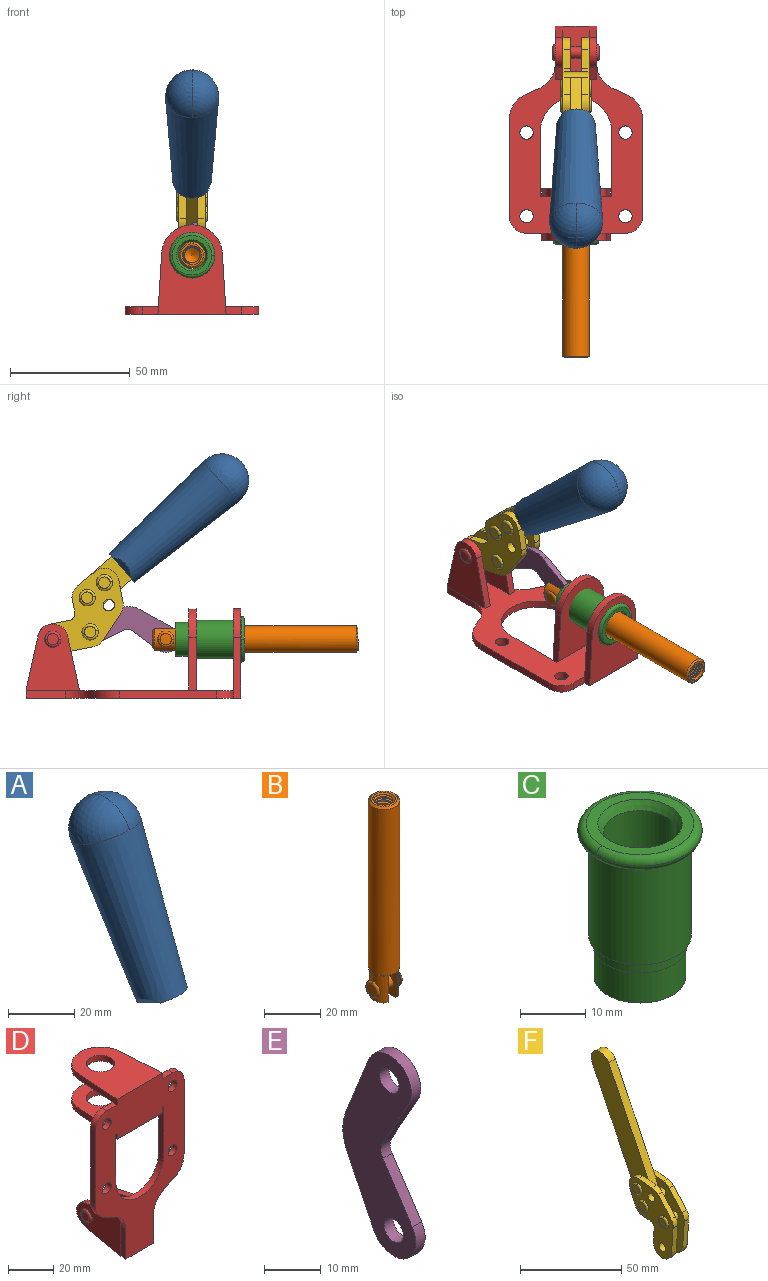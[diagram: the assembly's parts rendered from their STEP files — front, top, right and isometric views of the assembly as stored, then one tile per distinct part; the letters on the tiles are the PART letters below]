
ASSEMBLY  parts=6 mates=7
PART A: 11 faces, bbox 22.3x42.6x64.5 mm
  f0: sphere r=11.13mm, area 411.4mm2, adj f1,f8
  f1: cone r=11.11mm half-angle=3.3deg, axis (0,0.44,0.9), area 3251.8mm2, adj f0,f7,f8,f9,f10
  f2: cylinder r=6.16mm len=11.7mm, axis (1,0,0), area 89.5mm2, adj f3,f4,f5,f6
  f3: plane 60.23x36.75mm, normal (-1,0,0), area 763.6mm2, adj f2,f4,f6,f10
  f4: plane 51.37x25.05mm, normal (0,0.9,-0.44), area 264.2mm2, adj f2,f3,f5,f10
  f5: plane 60.23x36.75mm, normal (1,0,0), area 763.6mm2, adj f2,f4,f6,f10
  f6: plane 51.37x25.05mm, normal (0,-0.9,0.44), area 264.2mm2, adj f2,f3,f5,f10
  f7: plane 9.95x5.95mm, normal (0.71,-0.31,-0.64), area 25.8mm2, adj f1,f10
  f8: sphere r=11.13mm, area 411.4mm2, adj f0,f1
  f9: plane 9.95x5.95mm, normal (-0.71,-0.31,-0.64), area 25.8mm2, adj f1,f10
  f10: plane 14.27x11.38mm, normal (0,-0.44,-0.9), area 106.7mm2, adj f1,f3,f4,f5,f6,f7,f9
PART B: 48 faces, bbox 12.6x11.1x86.1 mm
  f0: torus R=2.41mm, axis (-1,0,0), area 15mm2, adj f30,f32,f34
  f1: torus R=2.41mm, axis (-1,0,0), area 15mm2, adj f29,f31,f33
  f2: cylinder r=5.54mm len=72.39mm, axis (0,0,1), area 2518.5mm2, adj f3,f4,f42,f43
  f3: cone r=5.54mm half-angle=45deg, axis (0,0,1), area 7.6mm2, adj f2,f5,f41
  f4: cone r=5.54mm half-angle=45deg, axis (0,0,-1), area 34.9mm2, adj f2,f39
  f5: cylinder r=5.08mm len=11.48mm, axis (0,0,1), area 108.3mm2, adj f3,f7,f8,f41
  f6: cylinder r=2.41mm len=4.83mm, axis (-1,0,0), area 71.2mm2, adj f40,f41
  f7: cylinder r=2.41mm len=4.83mm, axis (-1,0,0), area 7.6mm2, adj f5,f34
  f8: cone r=5.08mm half-angle=45deg, axis (0,0,1), area 10.6mm2, adj f5,f37,f41
  f9: cone r=3.98mm half-angle=45deg, axis (0,0,1), area 17.6mm2, adj f27,f39,f45,f46,f47
  f10: cylinder r=2.41mm len=4.83mm, axis (-1,0,0), area 7.6mm2, adj f33,f38
  f11: cylinder r=3.2mm len=6.4mm, axis (0,0,1), area 78.4mm2, adj f12,f28,f44,f45,f47
  f12: cylinder r=3.2mm len=6.4mm, axis (0,0,1), area 10.5mm2, adj f11,f13,f45,f47
  f13: cylinder r=3.2mm len=6.4mm, axis (0,0,1), area 10.5mm2, adj f12,f14,f45,f47
  f14: cylinder r=3.2mm len=6.4mm, axis (0,0,1), area 10.5mm2, adj f13,f15,f45,f47
  f15: cylinder r=3.2mm len=6.4mm, axis (0,0,1), area 10.5mm2, adj f14,f16,f45,f47
  f16: cylinder r=3.2mm len=6.4mm, axis (0,0,1), area 10.5mm2, adj f15,f17,f45,f47
  f17: cylinder r=3.2mm len=6.4mm, axis (0,0,1), area 10.5mm2, adj f16,f18,f45,f47
  f18: cylinder r=3.2mm len=6.4mm, axis (0,0,1), area 10.5mm2, adj f17,f19,f45,f47
  f19: cylinder r=3.2mm len=6.4mm, axis (0,0,1), area 10.5mm2, adj f18,f20,f45,f47
  f20: cylinder r=3.2mm len=6.4mm, axis (0,0,1), area 10.5mm2, adj f19,f21,f45,f47
  f21: cylinder r=3.2mm len=6.4mm, axis (0,0,1), area 10.5mm2, adj f20,f22,f45,f47
  f22: cylinder r=3.2mm len=6.4mm, axis (0,0,1), area 10.5mm2, adj f21,f23,f45,f47
  f23: cylinder r=3.2mm len=6.4mm, axis (0,0,1), area 10.5mm2, adj f22,f24,f45,f47
  f24: cylinder r=3.2mm len=6.4mm, axis (0,0,1), area 10.5mm2, adj f23,f25,f45,f47
  f25: cylinder r=3.2mm len=6.4mm, axis (0,0,1), area 10.5mm2, adj f24,f26,f45,f47
  f26: cylinder r=3.2mm len=6.4mm, axis (0,0,1), area 10.5mm2, adj f25,f27,f45,f47
  f27: cylinder r=3.2mm len=6.4mm, axis (0,0,1), area 7.4mm2, adj f9,f26,f45,f47
  f28: cone r=3.2mm half-angle=60deg, axis (0,0,1), area 37.2mm2, adj f11
  f29: plane 4.83x4.83mm, normal (-1,0,0), area 18.3mm2, adj f1,f31
  f30: plane 4.83x4.83mm, normal (1,0,0), area 18.3mm2, adj f0,f32
  f31: torus R=2.41mm, axis (-1,0,0), area 15mm2, adj f1,f29,f33
  f32: torus R=2.41mm, axis (-1,0,0), area 15mm2, adj f0,f30,f34
  f33: plane 6.83x6.83mm, normal (1,0,0), area 18.3mm2, adj f1,f10,f31
  f34: plane 6.83x6.83mm, normal (-1,0,0), area 18.3mm2, adj f0,f7,f32
  f35: cone r=5.08mm half-angle=45deg, axis (0,0,1), area 10.6mm2, adj f36,f38,f40
  f36: plane 7.25x1.97mm, normal (0,0,-1), area 10mm2, adj f35,f40
  f37: plane 7.25x1.97mm, normal (0,0,-1), area 10mm2, adj f8,f41
  f38: cylinder r=5.08mm len=11.48mm, axis (0,0,1), area 108.3mm2, adj f10,f35,f40,f42
  f39: plane 9.55x9.55mm, normal (0,0,1), area 22mm2, adj f4,f9
  f40: plane 12.76x10.09mm, normal (1,0,0), area 95.7mm2, adj f6,f35,f36,f38,f42,f43
  f41: plane 12.76x10.09mm, normal (-1,0,0), area 95.7mm2, adj f3,f5,f6,f8,f37,f43
  f42: cone r=5.54mm half-angle=45deg, axis (0,0,1), area 7.6mm2, adj f2,f38,f40
  f43: plane 11.07x4.7mm, normal (0,0,-1), area 50.4mm2, adj f2,f40,f41
  f44: plane 0.89x0.62mm, normal (-1,0,0), area 0.3mm2, adj f11,f45,f46,f47
  f45: bspline ~24.8x7.63mm, area 266.6mm2, adj f9,f11,f12,f13,f14,f15,f16,f17
  f46: bspline ~24.87x7.63mm, area 73.6mm2, adj f9,f44,f45,f47
  f47: bspline ~24.98x7.63mm, area 272.5mm2, adj f9,f11,f12,f13,f14,f15,f16,f17
PART C: 15 faces, bbox 20.6x20.6x28.7 mm
  f0: torus R=8.26mm, axis (0,0,1), area 56.8mm2, adj f1,f10,f12
  f1: torus R=8.26mm, axis (0,0,1), area 56.8mm2, adj f0,f6,f13
  f2: cylinder r=5.59mm len=25.91mm, axis (0,0,1), area 909.6mm2, adj f3,f4
  f3: cone r=6.86mm half-angle=45deg, axis (0,0,-1), area 70.2mm2, adj f2,f14
  f4: cone r=6.47mm half-angle=30deg, axis (0,0,1), area 66.7mm2, adj f2,f13
  f5: cylinder r=7.04mm len=14.07mm, axis (0,0,1), area 252.6mm2, adj f11,f14
  f6: torus R=8.26mm, axis (0,0,1), area 56.8mm2, adj f1,f12,f13
  f7: cylinder r=7.16mm len=14.33mm, axis (0,0,1), area 91.5mm2, adj f9,f11
  f8: cylinder r=7.86mm len=18.42mm, axis (0,0,1), area 909.6mm2, adj f9,f10
  f9: plane 15.72x15.72mm, normal (0,0,-1), area 33mm2, adj f7,f8
  f10: plane 16.51x16.51mm, normal (0,0,-1), area 19.9mm2, adj f0,f8,f12
  f11: plane 14.33x14.33mm, normal (0,0,-1), area 5.7mm2, adj f5,f7
  f12: torus R=8.26mm, axis (0,0,1), area 56.8mm2, adj f0,f6,f10
  f13: plane 16.51x16.51mm, normal (0,0,1), area 82.7mm2, adj f1,f4,f6
  f14: plane 14.07x14.07mm, normal (0,0,-1), area 7.8mm2, adj f3,f5
PART D: 55 faces, bbox 55.7x37.4x89.8 mm
  f0: torus R=2.41mm, axis (-1,0,0), area 15mm2, adj f11,f15,f25
  f1: torus R=2.41mm, axis (-1,0,0), area 15mm2, adj f10,f12,f22
  f2: cylinder r=2.78mm len=5.56mm, axis (0,-1,0), area 54.2mm2, adj f30,f54
  f3: cylinder r=14.99mm len=29.97mm, axis (0,-1,0), area 145.9mm2, adj f30,f49,f53,f54
  f4: cylinder r=2.78mm len=5.56mm, axis (0,-1,0), area 54.2mm2, adj f30,f54
  f5: cylinder r=2.78mm len=5.56mm, axis (0,-1,0), area 54.2mm2, adj f30,f54
  f6: cylinder r=2.78mm len=5.56mm, axis (0,-1,0), area 54.2mm2, adj f30,f54
  f7: cylinder r=6.35mm len=12.7mm, axis (0,0,1), area 123.6mm2, adj f27,f51
  f8: cylinder r=6.35mm len=12.7mm, axis (0,0,-1), area 124.7mm2, adj f21,f35
  f9: cylinder r=2.41mm len=11.18mm, axis (-1,0,0), area 169.4mm2, adj f16,f19
  f10: plane 4.83x4.83mm, normal (1,0,0), area 18.3mm2, adj f1,f12
  f11: plane 4.83x4.83mm, normal (-1,0,0), area 18.3mm2, adj f0,f15
  f12: torus R=2.41mm, axis (-1,0,0), area 15mm2, adj f1,f10,f22
  f13: cylinder r=6.35mm len=12.41mm, axis (1,0,0), area 53.4mm2, adj f18,f19,f22,f23
  f14: cylinder r=6.35mm len=12.41mm, axis (-1,0,0), area 53.4mm2, adj f16,f17,f24,f25
  f15: torus R=2.41mm, axis (-1,0,0), area 15mm2, adj f0,f11,f25
  f16: plane 27.86x22.35mm, normal (1,0,0), area 425.4mm2, adj f9,f14,f17,f24,f30
  f17: plane 22.86x4.97mm, normal (0,0.21,0.98), area 72.5mm2, adj f14,f16,f25,f30
  f18: plane 22.86x4.97mm, normal (0,0.21,0.98), area 72.5mm2, adj f13,f19,f22,f30
  f19: plane 27.86x22.35mm, normal (-1,0,0), area 425.4mm2, adj f9,f13,f18,f23,f30
  f20: cylinder r=12.7mm len=25.35mm, axis (0,0,-1), area 119.8mm2, adj f21,f34,f35,f36
  f21: plane 34.21x28.07mm, normal (0,0,-1), area 702.4mm2, adj f8,f20,f30,f34,f36
  f22: plane 27.96x22.45mm, normal (1,0,0), area 407.2mm2, adj f1,f12,f13,f18,f23,f30,f42,f43
  f23: plane 22.86x4.97mm, normal (0,0.21,-0.98), area 72.5mm2, adj f13,f19,f22,f44
  f24: plane 22.86x4.97mm, normal (0,0.21,-0.98), area 72.5mm2, adj f14,f16,f25,f44
  f25: plane 27.86x22.35mm, normal (-1,0,0), area 407.1mm2, adj f0,f14,f15,f17,f24,f30,f45,f46
  f26: plane 3.1x0.95mm, normal (0,0,-1), area 2.7mm2, adj f30,f49,f50,f54
  f27: plane 34.21x28.07mm, normal (0,0,1), area 702.4mm2, adj f7,f28,f30,f50,f52
  f28: cylinder r=12.7mm len=25.35mm, axis (0,0,1), area 118.8mm2, adj f27,f50,f51,f52
  f29: plane 3.1x0.95mm, normal (0,0,-1), area 2.7mm2, adj f30,f52,f53,f54
  f30: plane 86.54x55.63mm, normal (0,1,0), area 2362.9mm2, adj f2,f3,f4,f5,f6,f16,f17,f18
  f31: plane 40.56x3.1mm, normal (-1,0,0), area 125.7mm2, adj f30,f32,f48,f54
  f32: cylinder r=7.11mm len=7.11mm, axis (0,-1,0), area 34.6mm2, adj f30,f31,f33,f54
  f33: plane 6.67x3.1mm, normal (0,0,1), area 20.4mm2, adj f30,f32,f34,f54
  f34: plane 25.39x3.13mm, normal (-1,0.06,0), area 79.5mm2, adj f20,f21,f33,f35,f54
  f35: plane 37.31x28.45mm, normal (0,0,1), area 789.9mm2, adj f8,f20,f34,f36,f54
  f36: plane 25.39x3.13mm, normal (1,0.06,0), area 79.5mm2, adj f20,f21,f35,f37,f54
  f37: plane 6.67x3.1mm, normal (0,0,1), area 20.4mm2, adj f30,f36,f38,f54
  f38: cylinder r=7.11mm len=7.11mm, axis (0,-1,0), area 34.6mm2, adj f30,f37,f39,f54
  f39: plane 40.56x3.1mm, normal (1,0,0), area 125.7mm2, adj f30,f38,f40,f54
  f40: cylinder r=11.18mm len=10.16mm, axis (0,-1,0), area 39.5mm2, adj f30,f39,f41,f54
  f41: plane 6.09x3.1mm, normal (0.42,0,-0.91), area 20.8mm2, adj f30,f40,f42,f54
  f42: cylinder r=11.18mm len=9.41mm, axis (0,-1,0), area 37.2mm2, adj f22,f30,f41,f43,f54
  f43: plane 16.5x3.1mm, normal (1,0,0), area 51.1mm2, adj f22,f42,f44,f54
  f44: plane 17.37x3.1mm, normal (0,0,-1), area 53.8mm2, adj f23,f24,f30,f43,f45,f54
  f45: plane 16.5x3.1mm, normal (-1,0,0), area 51.1mm2, adj f25,f44,f46,f54
  f46: cylinder r=11.18mm len=9.41mm, axis (0,-1,0), area 37.2mm2, adj f25,f30,f45,f47,f54
  f47: plane 6.09x3.1mm, normal (-0.42,0,-0.91), area 20.8mm2, adj f30,f46,f48,f54
  f48: cylinder r=11.18mm len=10.16mm, axis (0,-1,0), area 39.5mm2, adj f30,f31,f47,f54
  f49: plane 26.54x3.1mm, normal (-1,0,0), area 82.3mm2, adj f3,f26,f30,f54
  f50: plane 25.39x3.1mm, normal (1,0.06,0), area 78.8mm2, adj f26,f27,f28,f51,f54
  f51: plane 37.31x28.45mm, normal (0,0,-1), area 789.9mm2, adj f7,f28,f50,f52,f54
  f52: plane 25.39x3.1mm, normal (-1,0.06,0), area 78.8mm2, adj f27,f28,f29,f51,f54
  f53: plane 26.54x3.1mm, normal (1,0,0), area 82.3mm2, adj f3,f29,f30,f54
  f54: plane 89.66x55.63mm, normal (0,-1,0), area 2678.5mm2, adj f2,f3,f4,f5,f6,f26,f29,f31
PART E: 12 faces, bbox 2.3x18.2x42.8 mm
  f0: cylinder r=2.4mm len=4.8mm, axis (1,0,0), area 34.9mm2, adj f4,f11
  f1: cylinder r=10.41mm len=8.47mm, axis (1,0,0), area 20.2mm2, adj f4,f9,f10,f11
  f2: cylinder r=3.05mm len=3.16mm, axis (1,0,0), area 7.7mm2, adj f4,f6,f7,f11
  f3: cylinder r=2.4mm len=4.8mm, axis (1,0,0), area 34.9mm2, adj f4,f11
  f4: plane 42.81x18.23mm, normal (-1,0,0), area 414.1mm2, adj f0,f1,f2,f3,f5,f6,f7,f8
  f5: cylinder r=5.54mm len=10.67mm, axis (1,0,0), area 41.8mm2, adj f4,f6,f10,f11
  f6: plane 11.66x6.53mm, normal (0,-0.87,-0.49), area 30.9mm2, adj f2,f4,f5,f11
  f7: plane 11.17x7.33mm, normal (0,-0.84,0.55), area 30.9mm2, adj f2,f4,f8,f11
  f8: cylinder r=5.54mm len=10.51mm, axis (1,0,0), area 41.8mm2, adj f4,f7,f9,f11
  f9: plane 13.67x6.67mm, normal (0,0.9,-0.44), area 35.1mm2, adj f1,f4,f8,f11
  f10: plane 14.1x5.7mm, normal (0,0.93,0.37), area 35.1mm2, adj f1,f4,f5,f11
  f11: plane 42.81x18.23mm, normal (1,0,0), area 414.1mm2, adj f0,f1,f2,f3,f5,f6,f7,f8
PART F: 59 faces, bbox 12.9x60.2x99.6 mm
  f0: torus R=2.39mm, axis (-1,0,0), area 14.9mm2, adj f20,f43,f51
  f1: torus R=2.39mm, axis (-1,0,0), area 14.9mm2, adj f19,f42,f51
  f2: torus R=2.39mm, axis (-1,0,0), area 14.9mm2, adj f18,f35,f51
  f3: torus R=2.39mm, axis (-1,0,0), area 14.9mm2, adj f14,f17,f23
  f4: torus R=2.39mm, axis (-1,0,0), area 14.9mm2, adj f13,f16,f23
  f5: torus R=2.39mm, axis (-1,0,0), area 14.9mm2, adj f12,f15,f23
  f6: cylinder r=2.39mm len=4.78mm, axis (1,0,0), area 46.5mm2, adj f48,f50,f51
  f7: cylinder r=2.39mm len=4.78mm, axis (1,0,0), area 46.5mm2, adj f50,f51
  f8: cylinder r=6.35mm len=12.68mm, axis (1,0,0), area 61.8mm2, adj f38,f39,f50,f51
  f9: cylinder r=2.39mm len=4.78mm, axis (-1,0,0), area 70.5mm2, adj f46,f50
  f10: cylinder r=2.39mm len=4.78mm, axis (-1,0,0), area 46.5mm2, adj f23,f45,f46
  f11: cylinder r=2.39mm len=4.78mm, axis (-1,0,0), area 46.5mm2, adj f23,f46
  f12: plane 4.78x4.78mm, normal (1,0,0), area 17.9mm2, adj f5,f15
  f13: plane 4.78x4.78mm, normal (1,0,0), area 17.9mm2, adj f4,f16
  f14: plane 4.78x4.78mm, normal (1,0,0), area 17.9mm2, adj f3,f17
  f15: torus R=2.39mm, axis (-1,0,0), area 14.9mm2, adj f5,f12,f23
  f16: torus R=2.39mm, axis (-1,0,0), area 14.9mm2, adj f4,f13,f23
  f17: torus R=2.39mm, axis (-1,0,0), area 14.9mm2, adj f3,f14,f23
  f18: plane 4.78x4.78mm, normal (-1,0,0), area 17.9mm2, adj f2,f35
  f19: plane 4.78x4.78mm, normal (-1,0,0), area 17.9mm2, adj f1,f42
  f20: plane 4.78x4.78mm, normal (-1,0,0), area 17.9mm2, adj f0,f43
  f21: plane 2.26x0.2mm, normal (1,0,0), area 0.2mm2, adj f31,f44
  f22: plane 2.26x0.2mm, normal (-1,0,0), area 0.2mm2, adj f41,f44
  f23: plane 39.37x30.77mm, normal (1,0,0), area 565.5mm2, adj f3,f4,f5,f10,f11,f15,f16,f17
  f24: cylinder r=6.1mm len=4.15mm, axis (-1,0,0), area 14.7mm2, adj f23,f25,f32,f46
  f25: plane 10.25x9.01mm, normal (0,-0.75,0.66), area 42.3mm2, adj f23,f24,f26,f46
  f26: cylinder r=6.35mm len=4.64mm, axis (-1,0,0), area 15.6mm2, adj f23,f25,f27,f46
  f27: plane 15.84x3.1mm, normal (0,-1,-0.07), area 49.2mm2, adj f23,f26,f28,f46
  f28: cylinder r=6.35mm len=12.68mm, axis (-1,0,0), area 61.8mm2, adj f23,f27,f29,f46
  f29: plane 8.11x3.1mm, normal (0,1,0.07), area 25.2mm2, adj f23,f28,f30,f46
  f30: cylinder r=3.05mm len=3.25mm, axis (-1,0,0), area 14.8mm2, adj f23,f29,f31,f46
  f31: plane 5.99x3.1mm, normal (0,0.07,-1), area 18.6mm2, adj f21,f23,f30,f44,f46
  f32: plane 9.5x3.1mm, normal (0,-0.07,1), area 29.5mm2, adj f23,f24,f33,f46,f47
  f33: cylinder r=6.1mm len=8.63mm, axis (-1,0,0), area 39.1mm2, adj f23,f32,f34,f47
  f34: plane 8.65x3.96mm, normal (0,0.91,-0.42), area 29.5mm2, adj f23,f33,f44,f47
  f35: torus R=2.39mm, axis (-1,0,0), area 14.9mm2, adj f2,f18,f51
  f36: plane 10.25x9.01mm, normal (0,-0.75,0.66), area 42.3mm2, adj f37,f49,f50,f51
  f37: cylinder r=6.35mm len=4.64mm, axis (1,0,0), area 15.6mm2, adj f36,f38,f50,f51
  f38: plane 15.84x3.1mm, normal (0,-1,-0.07), area 49.2mm2, adj f8,f37,f50,f51
  f39: plane 8.11x3.1mm, normal (0,1,0.07), area 25.2mm2, adj f8,f40,f50,f51
  f40: cylinder r=3.05mm len=3.25mm, axis (1,0,0), area 14.8mm2, adj f39,f41,f50,f51
  f41: plane 5.99x3.1mm, normal (0,0.07,-1), area 18.6mm2, adj f22,f40,f44,f50,f51
  f42: torus R=2.39mm, axis (-1,0,0), area 14.9mm2, adj f1,f19,f51
  f43: torus R=2.39mm, axis (-1,0,0), area 14.9mm2, adj f0,f20,f51
  f44: cylinder r=6.35mm len=12.12mm, axis (-1,0,0), area 128.9mm2, adj f21,f22,f23,f31,f34,f41,f46,f47
  f45: plane 2.65x1.35mm, normal (1,0,0), area 1mm2, adj f10,f55
  f46: plane 39.08x20.42mm, normal (-1,0,0), area 412.5mm2, adj f9,f10,f11,f24,f25,f26,f27,f28
  f47: plane 77.62x39.82mm, normal (1,0,0), area 850mm2, adj f32,f33,f34,f44,f53,f54,f55
  f48: plane 2.65x1.35mm, normal (-1,0,0), area 1mm2, adj f6,f55
  f49: cylinder r=6.1mm len=4.15mm, axis (1,0,0), area 14.7mm2, adj f36,f50,f51,f56
  f50: plane 39.08x20.42mm, normal (1,0,0), area 412.5mm2, adj f6,f7,f8,f9,f36,f37,f38,f39
  f51: plane 39.37x30.77mm, normal (-1,0,0), area 565.5mm2, adj f0,f1,f2,f6,f7,f8,f35,f36
  f52: plane 8.65x3.96mm, normal (0,0.91,-0.42), area 29.5mm2, adj f44,f51,f57,f58
  f53: plane 68.49x33.4mm, normal (0,0.9,-0.44), area 358.1mm2, adj f44,f47,f54,f58
  f54: cylinder r=6.35mm len=12.06mm, axis (1,0,0), area 93.7mm2, adj f47,f53,f55,f58
  f55: plane 68.49x33.4mm, normal (0,-0.9,0.44), area 358.1mm2, adj f44,f45,f46,f47,f48,f50,f54,f58
  f56: plane 9.5x3.1mm, normal (0,-0.07,1), area 29.5mm2, adj f49,f50,f51,f57,f58
  f57: cylinder r=6.1mm len=8.63mm, axis (1,0,0), area 39.1mm2, adj f51,f52,f56,f58
  f58: plane 77.62x39.82mm, normal (-1,0,0), area 850mm2, adj f44,f52,f53,f54,f55,f56,f57
PLACE A rot(axis=(1,0,0),75deg) t=(0.04,19.4,9.14)mm
PLACE B rot(axis=(1,0,0),90deg) t=(0,25.05,0)mm
PLACE C rot(axis=(1,0,0),90deg) t=(0,25.69,0)mm
PLACE D rot(axis=(1,0,0),90deg) t=(0,24.68,0)mm fixed
PLACE E rot(axis=(1,0,0),97.5deg) t=(1.16,28.12,2.22)mm
PLACE F rot(axis=(1,0,0),75deg) t=(0,19.4,9.14)mm
MATE revolute E.f3 <-> F.f4  axis (1,0,0) through (0,41.19,27.64)mm
MATE fastened A.f2 <-> A.f1  axis (1,0,0) through (-2.27,-15.12,91.94)mm
MATE fastened C.f2 <-> D.f7  axis (0,1,0) through (0,-21.72,24.61)mm
MATE slider B.f2 <-> C.f2  axis (0,-1,0) through (0,-33.73,24.61)mm
MATE revolute E.f0 <-> B.f6  axis (-1,0,0) through (0,9.58,24.61)mm
MATE revolute D.f0 <-> F.f7  axis (-1,0,0) through (0,56.77,24.61)mm
MATE fastened A.f2 <-> F.f54  axis (-1,0,0) through (2.35,-15.12,91.94)mm
